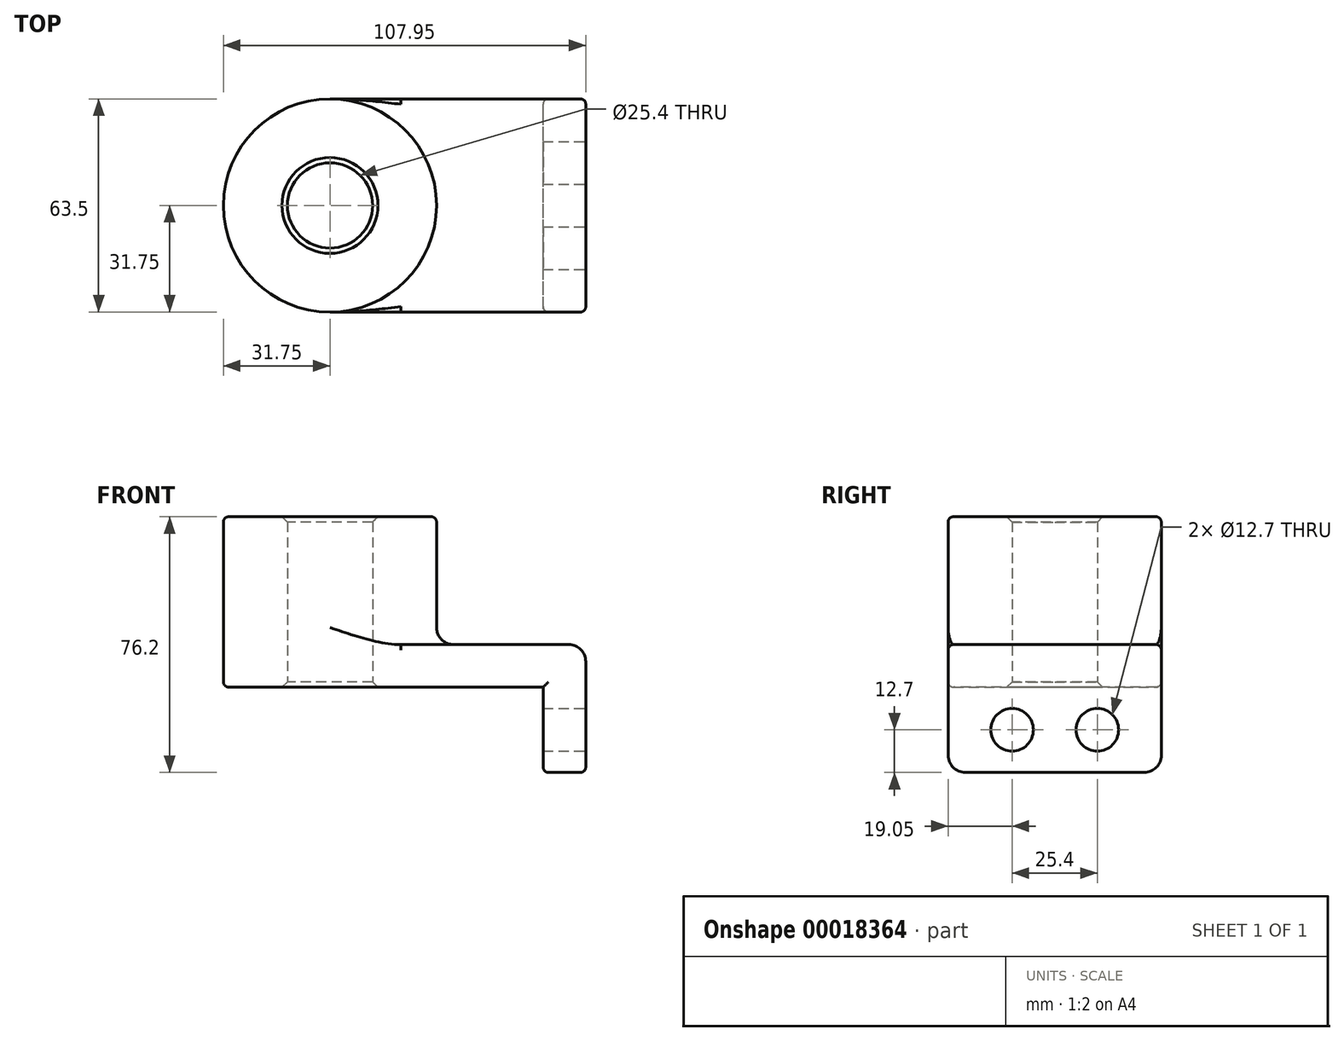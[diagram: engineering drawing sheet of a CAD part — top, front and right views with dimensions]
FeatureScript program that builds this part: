
annotation { "Feature Type Name" : "Feature", "Feature Type Description" : "" }
export const myFeature = defineFeature(function(context is Context, id is Id, definition is map)
    precondition{}
    {
        {
            var Q0;
            Q0=qCreatedBy(makeId("Top.planeOp"),FACE);
            var sketch = newSketch(context, id + "F0", { "sketchPlane" : qUnion([Q0])});
            skLineSegment(sketch, "E0.rect.bottom", {"start": v(-38.1, -31.75) * mm, "end": v(38.1, -31.75) * mm});
            skLineSegment(sketch, "E0.rect.top", {"start": v(-38.1, 31.75) * mm, "end": v(38.1, 31.75) * mm});
            skLineSegment(sketch, "E0.rect.left", {"start": v(-38.1, -31.75) * mm, "end": v(-38.1, 31.75) * mm});
            skLineSegment(sketch, "E0.rect.right", {"start": v(38.1, -31.75) * mm, "end": v(38.1, 31.75) * mm});
            skPoint(sketch, "E0.rect.middle", {"position": v(0, 0) * mm});
            skCircle(sketch, "E1", {"center": v(-38.1, 0) * mm, "radius": 31.75 * mm});
            skCircle(sketch, "E2", {"center": v(-38.1, 0) * mm, "radius": 12.7 * mm});
            skSolve(sketch);
        }
        {
            var Q0;
            {var subQ3=sQuery(id+"F0.wireOp",EDGE,"E0.rect.bottom");Q0=makeQuery(id+"F0.imprint","IMPRINT",FACE,{"disambiguationData":[TD([[makeQuery(id+"F0.imprint","IMPRINT",EDGE,{"derivedFrom":subQ3}),1.0]])]});}
            var Q1;
            {var subQ0=sQuery(id+"F0.wireOp",EDGE,"E2");var subQ1=sQuery(id+"F0.wireOp",EDGE,"E0.rect.left");var subQ3=makeQuery(id+"F0.imprint","INTERSECT",VERTEX,{"disambiguationData":[OD(0.0)],"derivedFrom":[subQ1,subQ0]});Q1=makeQuery(id+"F0.imprint","IMPRINT",FACE,{"disambiguationData":[TD([[makeQuery(id+"F0.imprint","IMPRINT",EDGE,{"disambiguationData":[TD([[subQ3,1.0]])],"derivedFrom":subQ0}),-1.0]])]});}
            var Q2;
            {var subQ0=sQuery(id+"F0.wireOp",EDGE,"E2");var subQ1=sQuery(id+"F0.wireOp",EDGE,"E0.rect.left");var subQ3=makeQuery(id+"F0.imprint","INTERSECT",VERTEX,{"disambiguationData":[OD(0.0)],"derivedFrom":[subQ1,subQ0]});Q2=makeQuery(id+"F0.imprint","IMPRINT",FACE,{"disambiguationData":[TD([[makeQuery(id+"F0.imprint","IMPRINT",EDGE,{"disambiguationData":[TD([[subQ3,-1.0]])],"derivedFrom":subQ0}),-1.0]])]});}
            extrude(context, id + "F1", {"entities" : qUnion([Q0, Q1, Q2]), "depth" : 12.7 * mm});
        }
        {
            var Q0;
            {var subQ0=sQuery(id+"F0.wireOp",EDGE,"E2");var subQ1=sQuery(id+"F0.wireOp",EDGE,"E0.rect.left");var subQ3=makeQuery(id+"F0.imprint","INTERSECT",VERTEX,{"disambiguationData":[OD(0.0)],"derivedFrom":[subQ1,subQ0]});Q0=makeQuery(id+"F0.imprint","IMPRINT",FACE,{"disambiguationData":[TD([[makeQuery(id+"F0.imprint","IMPRINT",EDGE,{"disambiguationData":[TD([[subQ3,1.0]])],"derivedFrom":subQ0}),-1.0]])]});}
            var Q1;
            {var subQ0=sQuery(id+"F0.wireOp",EDGE,"E2");var subQ1=sQuery(id+"F0.wireOp",EDGE,"E0.rect.left");var subQ3=makeQuery(id+"F0.imprint","INTERSECT",VERTEX,{"disambiguationData":[OD(0.0)],"derivedFrom":[subQ1,subQ0]});Q1=makeQuery(id+"F0.imprint","IMPRINT",FACE,{"disambiguationData":[TD([[makeQuery(id+"F0.imprint","IMPRINT",EDGE,{"disambiguationData":[TD([[subQ3,-1.0]])],"derivedFrom":subQ0}),-1.0]])]});}
            extrude(context, id + "F2", {"entities" : qUnion([Q0, Q1]), "operationType" : NewBodyOperationType.ADD, "depth" : 50.8 * mm});
        }
        {
            var Q0;
            Q0=makeQuery(id+"F1.opExtrude","SWEPT_FACE",FACE,{"disambiguationData":[OSD([sQuery(id+"F0.wireOp",EDGE,"E0.rect.right")])]});
            var sketch = newSketch(context, id + "F3", { "sketchPlane" : qUnion([Q0])});
            skLineSegment(sketch, "E3.bottom", {"start": v(-31.75, 12.7) * mm, "end": v(31.75, 12.7) * mm});
            skLineSegment(sketch, "E3.top", {"start": v(-31.75, -25.4) * mm, "end": v(31.75, -25.4) * mm});
            skLineSegment(sketch, "E3.left", {"start": v(-31.75, 12.7) * mm, "end": v(-31.75, -25.4) * mm});
            skLineSegment(sketch, "E3.right", {"start": v(31.75, 12.7) * mm, "end": v(31.75, -25.4) * mm});
            skCircle(sketch, "E4", {"center": v(-12.7, -12.7) * mm, "radius": 6.35 * mm});
            skLineSegment(sketch, "E5", {"start": v(0, 0) * mm, "end": v(0, -25.4) * mm, "construction": true});
            skCircle(sketch, "E6.MirrorC", {"center": v(12.7, -12.7) * mm, "radius": 6.35 * mm});
            skSolve(sketch);
        }
        {
            var Q0;
            Q0 = qSketchRegion(id + "F3", true);
            extrude(context, id + "F4", {"entities" : qUnion([Q0]), "operationType" : NewBodyOperationType.ADD, "oppositeDirection" : true, "depth" : 12.7 * mm});
        }
        {
            var Q0;
            {var subQ0=sQuery(id+"F0.wireOp",EDGE,"E1");Q0=makeQuery(id+"F2.boolean.opBoolean","INTERSECT",EDGE,{"derivedFrom":[makeQuery(id+"F1.opExtrude","CAP_FACE",FACE,{"disambiguationData":[OSD([sQuery(id+"F0.wireOp",EDGE,"E0.rect.bottom"),sQuery(id+"F0.wireOp",EDGE,"E0.rect.top"),sQuery(id+"F0.wireOp",EDGE,"E0.rect.right"),subQ0,sQuery(id+"F0.wireOp",EDGE,"E2")])],"isStart":false}),makeQuery(id+"F2.opExtrude","SWEPT_FACE",FACE,{"disambiguationData":[OSD([subQ0])]})]});}
            var Q1;
            Q1=makeQuery(id+"F1.opExtrude","CAP_EDGE",EDGE,{"disambiguationData":[OSD([sQuery(id+"F0.wireOp",EDGE,"E0.rect.right")])],"isStart":false});
            var Q2;
            Q2=makeQuery(id+"F4.opExtrude","SWEPT_EDGE",EDGE,{"disambiguationData":[OSD([sQuery(id+"F3.wireOp",EDGE,"E3.top"),sQuery(id+"F3.wireOp",EDGE,"E3.right")])]});
            var Q3;
            Q3=makeQuery(id+"F4.opExtrude","SWEPT_EDGE",EDGE,{"disambiguationData":[OSD([sQuery(id+"F3.wireOp",EDGE,"E3.top"),sQuery(id+"F3.wireOp",EDGE,"E3.left")])]});
            fillet(context, id + "F5", {"entities" : qUnion([Q0, Q1, Q2, Q3]), "radius" : 5.08 * mm, "tangentPropagation" : true, "allowEdgeOverflow" : false});
        }
        {
            var Q0;
            Q0=makeQuery(id+"F2.opExtrude","CAP_EDGE",EDGE,{"disambiguationData":[OSD([sQuery(id+"F0.wireOp",EDGE,"E1")])],"isStart":false});
            var Q1;
            Q1=makeQuery(id+"F1.opExtrude","CAP_EDGE",EDGE,{"disambiguationData":[OSD([sQuery(id+"F0.wireOp",EDGE,"E0.rect.bottom")])],"isStart":false});
            var Q2;
            Q2=makeQuery(id+"F1.opExtrude","CAP_EDGE",EDGE,{"disambiguationData":[OSD([sQuery(id+"F0.wireOp",EDGE,"E0.rect.top")])],"isStart":false});
            var Q3;
            Q3=makeQuery(id+"F1.opExtrude","CAP_EDGE",EDGE,{"disambiguationData":[OSD([sQuery(id+"F0.wireOp",EDGE,"E0.rect.top")])],"isStart":true});
            var Q4;
            Q4=makeQuery(id+"F4.opExtrude","CAP_EDGE",EDGE,{"disambiguationData":[OSD([sQuery(id+"F3.wireOp",EDGE,"E3.right")])],"isStart":false});
            var Q5;
            Q5=makeQuery(id+"F4.boolean.opBoolean","MERGE",EDGE,{"derivedFrom":[makeQuery(id+"F1.opExtrude","SWEPT_EDGE",EDGE,{"disambiguationData":[OSD([sQuery(id+"F0.wireOp",EDGE,"E0.rect.bottom"),sQuery(id+"F0.wireOp",EDGE,"E0.rect.right")])]}),makeQuery(id+"F4.opExtrude","CAP_EDGE",EDGE,{"disambiguationData":[OSD([sQuery(id+"F3.wireOp",EDGE,"E3.left")])],"isStart":true})]});
            fillet(context, id + "F6", {"entities" : qUnion([Q0, Q1, Q2, Q3, Q4, Q5]), "radius" : 1.59 * mm, "tangentPropagation" : true, "allowEdgeOverflow" : false});
        }
        {
            var Q0;
            {var subQ0=sQuery(id+"F0.wireOp",EDGE,"E2");Q0=makeQuery(id+"F2.boolean.opBoolean","MERGE",FACE,{"derivedFrom":[makeQuery(id+"F1.opExtrude","SWEPT_FACE",FACE,{"disambiguationData":[OSD([subQ0])]}),makeQuery(id+"F2.opExtrude","SWEPT_FACE",FACE,{"disambiguationData":[OSD([subQ0])]})]});}
            chamfer(context, id + "F7", {"entities" : qUnion([Q0]), "width" : 1.59 * mm, "tangentPropagation" : true});
        }
    });
